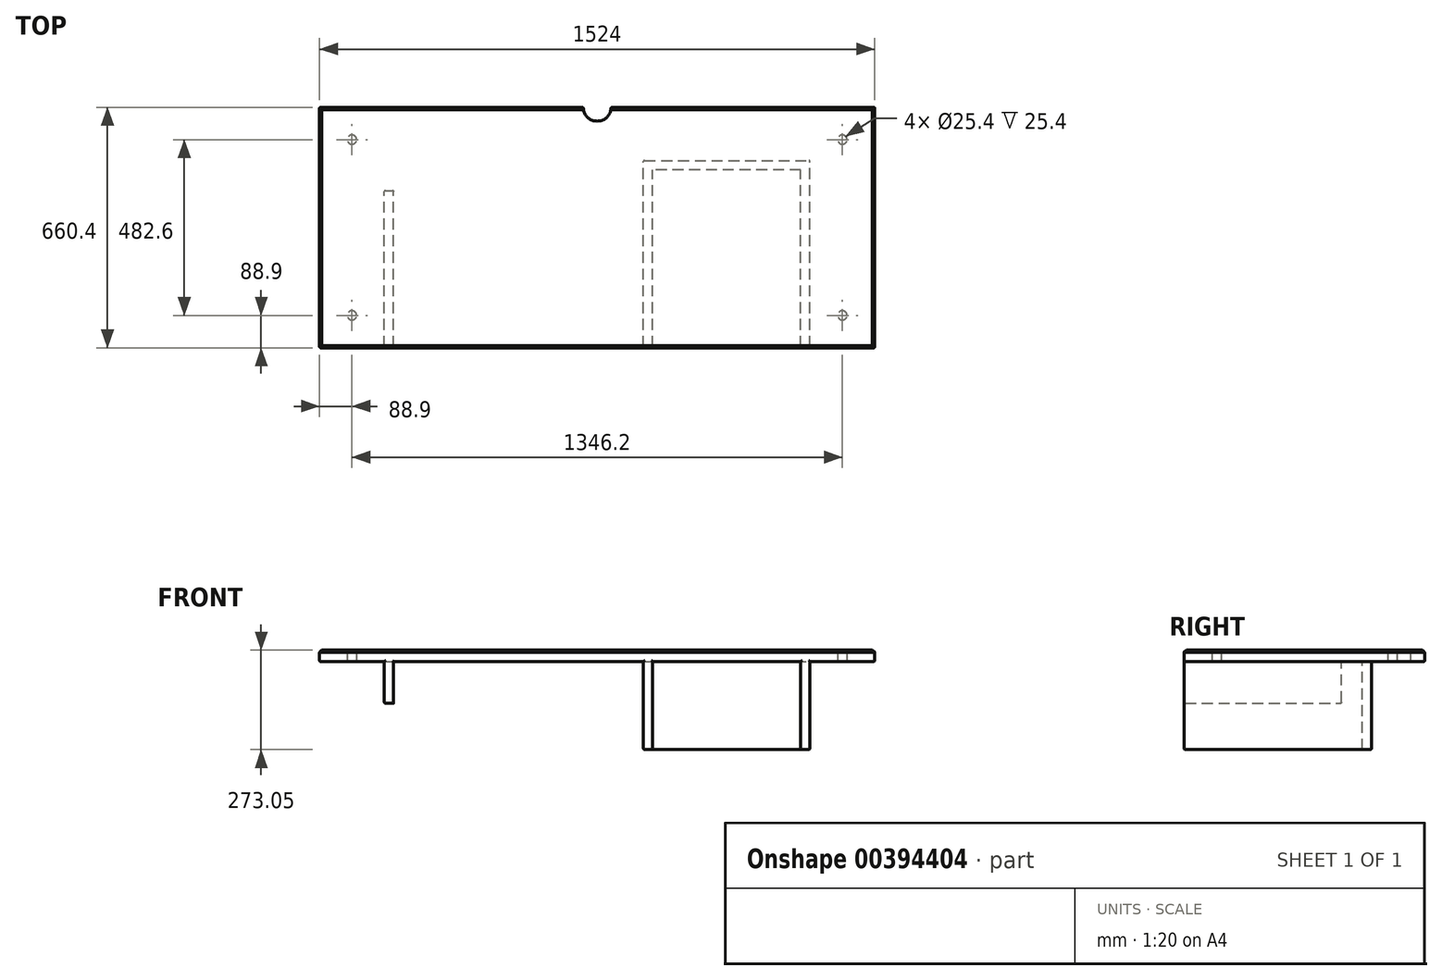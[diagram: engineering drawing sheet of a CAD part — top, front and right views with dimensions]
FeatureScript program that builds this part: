
annotation { "Feature Type Name" : "Feature", "Feature Type Description" : "" }
export const myFeature = defineFeature(function(context is Context, id is Id, definition is map)
    precondition{}
    {
        {
            var Q0;
            Q0=qCreatedBy(makeId("Top.planeOp"),FACE);
            var sketch = newSketch(context, id + "F0", { "sketchPlane" : qUnion([Q0])});
            skLineSegment(sketch, "E0.bottom", {"start": v(-762, 330.2) * mm, "end": v(762, 330.2) * mm});
            skLineSegment(sketch, "E0.top", {"start": v(-762, -330.2) * mm, "end": v(762, -330.2) * mm});
            skLineSegment(sketch, "E0.left", {"start": v(-762, 330.2) * mm, "end": v(-762, -330.2) * mm});
            skLineSegment(sketch, "E0.right", {"start": v(762, 330.2) * mm, "end": v(762, -330.2) * mm});
            skPoint(sketch, "E0.middle", {"position": v(0, 0) * mm});
            skSolve(sketch);
        }
        {
            var Q0;
            Q0 = qSketchRegion(id + "F0", true);
            extrude(context, id + "F1", {"entities" : qUnion([Q0]), "oppositeDirection" : true, "depth" : 31.75 * mm});
        }
        {
            var Q0;
            Q0=makeQuery(id+"F1.opExtrude","CAP_FACE",FACE,{"disambiguationData":[OSD([sQuery(id+"F0.wireOp",EDGE,"E0.bottom"),sQuery(id+"F0.wireOp",EDGE,"E0.top"),sQuery(id+"F0.wireOp",EDGE,"E0.left"),sQuery(id+"F0.wireOp",EDGE,"E0.right")])],"isStart":true});
            var sketch = newSketch(context, id + "F2", { "sketchPlane" : qUnion([Q0])});
            skCircle(sketch, "E1", {"center": v(0, 330.2) * mm, "radius": 38.1 * mm});
            skSolve(sketch);
        }
        {
            var Q0;
            Q0 = qSketchRegion(id + "F2", true);
            extrude(context, id + "F3", {"entities" : qUnion([Q0]), "operationType" : NewBodyOperationType.REMOVE, "endBound" : BoundingType.THROUGH_ALL, "oppositeDirection" : true, "depth" : 25.4 * mm});
        }
        {
            var Q0;
            Q0=makeQuery(id+"F1.opExtrude","CAP_FACE",FACE,{"disambiguationData":[OSD([sQuery(id+"F0.wireOp",EDGE,"E0.bottom"),sQuery(id+"F0.wireOp",EDGE,"E0.top"),sQuery(id+"F0.wireOp",EDGE,"E0.left"),sQuery(id+"F0.wireOp",EDGE,"E0.right")])],"isStart":false});
            var sketch = newSketch(context, id + "F4", { "sketchPlane" : qUnion([Q0])});
            skLineSegment(sketch, "E2.bottom", {"start": v(-584.2, 330.2) * mm, "end": v(-558.8, 330.2) * mm});
            skLineSegment(sketch, "E2.top", {"start": v(-584.2, -101.6) * mm, "end": v(-558.8, -101.6) * mm});
            skLineSegment(sketch, "E2.left", {"start": v(-584.2, 330.2) * mm, "end": v(-584.2, -101.6) * mm});
            skLineSegment(sketch, "E2.right", {"start": v(-558.8, 330.2) * mm, "end": v(-558.8, -101.6) * mm});
            skPoint(sketch, "E3.oppositeSnap0", {"position": v(-571.5, -101.6) * mm});
            skSolve(sketch);
        }
        {
            var Q0;
            Q0 = qSketchRegion(id + "F4", true);
            extrude(context, id + "F5", {"entities" : qUnion([Q0]), "operationType" : NewBodyOperationType.ADD, "depth" : 114.3 * mm});
        }
        {
            var Q0;
            {var subQ0=sQuery(id+"F0.wireOp",EDGE,"E0.bottom");var subQ1=sQuery(id+"F0.wireOp",EDGE,"E0.right");Q0=makeQuery(id+"F3.boolean.opBoolean","SPLIT",EDGE,{"disambiguationData":[TD([makeQuery(id+"F1.opExtrude","SWEPT_FACE",FACE,{"disambiguationData":[OSD([subQ1])]})])],"derivedFrom":makeQuery(id+"F1.opExtrude","CAP_EDGE",EDGE,{"disambiguationData":[OSD([subQ0])],"isStart":true})});}
            var Q1;
            Q1=makeQuery(id+"F1.opExtrude","CAP_EDGE",EDGE,{"disambiguationData":[OSD([sQuery(id+"F0.wireOp",EDGE,"E0.right")])],"isStart":true});
            var Q2;
            {var subQ0=sQuery(id+"F0.wireOp",EDGE,"E0.bottom");var subQ1=sQuery(id+"F0.wireOp",EDGE,"E0.left");Q2=makeQuery(id+"F3.boolean.opBoolean","SPLIT",EDGE,{"disambiguationData":[TD([makeQuery(id+"F1.opExtrude","SWEPT_FACE",FACE,{"disambiguationData":[OSD([subQ1])]})])],"derivedFrom":makeQuery(id+"F1.opExtrude","CAP_EDGE",EDGE,{"disambiguationData":[OSD([subQ0])],"isStart":true})});}
            var Q3;
            Q3=makeQuery(id+"F1.opExtrude","CAP_EDGE",EDGE,{"disambiguationData":[OSD([sQuery(id+"F0.wireOp",EDGE,"E0.left")])],"isStart":true});
            var Q4;
            Q4=makeQuery(id+"F1.opExtrude","CAP_EDGE",EDGE,{"disambiguationData":[OSD([sQuery(id+"F0.wireOp",EDGE,"E0.top")])],"isStart":true});
            var Q5;
            Q5=makeQuery(id+"F3.boolean.opBoolean","COPY",EDGE,{"derivedFrom":makeQuery(id+"F3.opExtrude","CAP_EDGE",EDGE,{"disambiguationData":[OSD([sQuery(id+"F2.wireOp",EDGE,"E1")])],"isStart":true})});
            chamfer(context, id + "F6", {"entities" : qUnion([Q0, Q1, Q2, Q3, Q4, Q5]), "width" : 6.35 * mm, "tangentPropagation" : true});
        }
        {
            var Q0;
            Q0=makeQuery(id+"F1.opExtrude","CAP_FACE",FACE,{"disambiguationData":[OSD([sQuery(id+"F0.wireOp",EDGE,"E0.bottom"),sQuery(id+"F0.wireOp",EDGE,"E0.top"),sQuery(id+"F0.wireOp",EDGE,"E0.left"),sQuery(id+"F0.wireOp",EDGE,"E0.right")])],"isStart":false});
            var sketch = newSketch(context, id + "F7", { "sketchPlane" : qUnion([Q0])});
            skCircle(sketch, "E4", {"center": v(-673.1, 241.3) * mm, "radius": 12.7 * mm});
            skCircle(sketch, "E5", {"center": v(-673.1, -241.3) * mm, "radius": 12.7 * mm});
            skCircle(sketch, "E6", {"center": v(673.1, 241.3) * mm, "radius": 12.7 * mm});
            skCircle(sketch, "E7", {"center": v(673.1, -241.3) * mm, "radius": 12.7 * mm});
            skSolve(sketch);
        }
        {
            var Q0;
            Q0 = qSketchRegion(id + "F7", true);
            extrude(context, id + "F8", {"entities" : qUnion([Q0]), "operationType" : NewBodyOperationType.REMOVE, "oppositeDirection" : true, "depth" : 25.4 * mm});
        }
        {
            var Q0;
            Q0=makeQuery(id+"F1.opExtrude","CAP_FACE",FACE,{"disambiguationData":[OSD([sQuery(id+"F0.wireOp",EDGE,"E0.bottom"),sQuery(id+"F0.wireOp",EDGE,"E0.top"),sQuery(id+"F0.wireOp",EDGE,"E0.left"),sQuery(id+"F0.wireOp",EDGE,"E0.right")])],"isStart":false});
            var sketch = newSketch(context, id + "F9", { "sketchPlane" : qUnion([Q0])});
            skLineSegment(sketch, "E8.bottom", {"start": v(127, 330.2) * mm, "end": v(152.4, 330.2) * mm});
            skLineSegment(sketch, "E8.top", {"start": v(127, -184.15) * mm, "end": v(152.4, -184.15) * mm});
            skLineSegment(sketch, "E8.left", {"start": v(127, 330.2) * mm, "end": v(127, -184.15) * mm});
            skLineSegment(sketch, "E8.right", {"start": v(152.4, 330.2) * mm, "end": v(152.4, -158.75) * mm});
            skLineSegment(sketch, "E9.bottom", {"start": v(558.8, 330.2) * mm, "end": v(584.2, 330.2) * mm});
            skLineSegment(sketch, "E9.top", {"start": v(558.8, -184.15) * mm, "end": v(584.2, -184.15) * mm});
            skLineSegment(sketch, "E9.left", {"start": v(558.8, 330.2) * mm, "end": v(558.8, -158.75) * mm});
            skLineSegment(sketch, "E9.right", {"start": v(584.2, 330.2) * mm, "end": v(584.2, -184.15) * mm});
            skLineSegment(sketch, "E10", {"start": v(584.2, -184.15) * mm, "end": v(127, -184.15) * mm});
            skLineSegment(sketch, "E11", {"start": v(558.8, -158.75) * mm, "end": v(152.4, -158.75) * mm});
            skSolve(sketch);
        }
        {
            var Q0;
            Q0 = qSketchRegion(id + "F9", true);
            extrude(context, id + "F10", {"entities" : qUnion([Q0]), "operationType" : NewBodyOperationType.ADD, "depth" : 241.3 * mm});
        }
        {
            var Q0;
            {var subQ0=sQuery(id+"F0.wireOp",EDGE,"E0.left");var subQ1=sQuery(id+"F0.wireOp",EDGE,"E0.top");Q0=makeQuery(id+"F5.boolean.opBoolean","SPLIT",EDGE,{"disambiguationData":[TD([makeQuery(id+"F1.opExtrude","SWEPT_FACE",FACE,{"disambiguationData":[OSD([subQ0])]})])],"derivedFrom":makeQuery(id+"F1.opExtrude","CAP_EDGE",EDGE,{"disambiguationData":[OSD([subQ1])],"isStart":false})});}
            var Q1;
            {var subQ0=sQuery(id+"F0.wireOp",EDGE,"E0.bottom");var subQ1=sQuery(id+"F0.wireOp",EDGE,"E0.right");Q1=makeQuery(id+"F3.boolean.opBoolean","SPLIT",EDGE,{"disambiguationData":[TD([makeQuery(id+"F1.opExtrude","SWEPT_FACE",FACE,{"disambiguationData":[OSD([subQ1])]})])],"derivedFrom":makeQuery(id+"F1.opExtrude","CAP_EDGE",EDGE,{"disambiguationData":[OSD([subQ0])],"isStart":false})});}
            var Q2;
            {var subQ0=sQuery(id+"F0.wireOp",EDGE,"E0.bottom");var subQ1=sQuery(id+"F0.wireOp",EDGE,"E0.left");Q2=makeQuery(id+"F3.boolean.opBoolean","SPLIT",EDGE,{"disambiguationData":[TD([makeQuery(id+"F1.opExtrude","SWEPT_FACE",FACE,{"disambiguationData":[OSD([subQ1])]})])],"derivedFrom":makeQuery(id+"F1.opExtrude","CAP_EDGE",EDGE,{"disambiguationData":[OSD([subQ0])],"isStart":false})});}
            var Q3;
            Q3=makeQuery(id+"F1.opExtrude","CAP_EDGE",EDGE,{"disambiguationData":[OSD([sQuery(id+"F0.wireOp",EDGE,"E0.left")])],"isStart":false});
            var Q4;
            Q4=makeQuery(id+"F1.opExtrude","CAP_EDGE",EDGE,{"disambiguationData":[OSD([sQuery(id+"F0.wireOp",EDGE,"E0.right")])],"isStart":false});
            var Q5;
            Q5=makeQuery(id+"F5.opExtrude","SWEPT_EDGE",EDGE,{"disambiguationData":[OSD([sQuery(id+"F0.wireOp",EDGE,"E0.top"),sQuery(id+"F4.wireOp",EDGE,"E2.bottom"),sQuery(id+"F4.wireOp",EDGE,"E2.left")])]});
            var Q6;
            Q6=makeQuery(id+"F5.opExtrude","SWEPT_EDGE",EDGE,{"disambiguationData":[OSD([sQuery(id+"F0.wireOp",EDGE,"E0.top"),sQuery(id+"F4.wireOp",EDGE,"E2.bottom"),sQuery(id+"F4.wireOp",EDGE,"E2.right")])]});
            var Q7;
            Q7=makeQuery(id+"F5.opExtrude","CAP_EDGE",EDGE,{"disambiguationData":[OSD([sQuery(id+"F4.wireOp",EDGE,"E2.bottom")])],"isStart":false});
            var Q8;
            Q8=makeQuery(id+"F5.opExtrude","SWEPT_EDGE",EDGE,{"disambiguationData":[OSD([sQuery(id+"F0.wireOp",EDGE,"E0.top"),sQuery(id+"F4.wireOp",EDGE,"E2.bottom"),sQuery(id+"F4.wireOp",EDGE,"E2.left")])]});
            var Q9;
            Q9=makeQuery(id+"F5.opExtrude","SWEPT_EDGE",EDGE,{"disambiguationData":[OSD([sQuery(id+"F0.wireOp",EDGE,"E0.top"),sQuery(id+"F4.wireOp",EDGE,"E2.bottom"),sQuery(id+"F4.wireOp",EDGE,"E2.right")])]});
            var Q10;
            Q10=makeQuery(id+"F5.opExtrude","SWEPT_EDGE",EDGE,{"disambiguationData":[OSD([sQuery(id+"F0.wireOp",EDGE,"E0.top"),sQuery(id+"F4.wireOp",EDGE,"E2.bottom"),sQuery(id+"F4.wireOp",EDGE,"E2.left")])]});
            var Q11;
            Q11=makeQuery(id+"F5.opExtrude","SWEPT_EDGE",EDGE,{"disambiguationData":[OSD([sQuery(id+"F0.wireOp",EDGE,"E0.top"),sQuery(id+"F4.wireOp",EDGE,"E2.bottom"),sQuery(id+"F4.wireOp",EDGE,"E2.right")])]});
            var Q12;
            Q12=makeQuery(id+"F5.opExtrude","SWEPT_EDGE",EDGE,{"disambiguationData":[OSD([sQuery(id+"F4.wireOp",EDGE,"E2.top"),sQuery(id+"F4.wireOp",EDGE,"E2.left")])]});
            var Q13;
            Q13=makeQuery(id+"F5.opExtrude","SWEPT_EDGE",EDGE,{"disambiguationData":[OSD([sQuery(id+"F4.wireOp",EDGE,"E2.top"),sQuery(id+"F4.wireOp",EDGE,"E2.right")])]});
            var Q14;
            Q14=makeQuery(id+"F5.opExtrude","CAP_EDGE",EDGE,{"disambiguationData":[OSD([sQuery(id+"F4.wireOp",EDGE,"E2.top")])],"isStart":false});
            var Q15;
            Q15=makeQuery(id+"F5.opExtrude","CAP_EDGE",EDGE,{"disambiguationData":[OSD([sQuery(id+"F4.wireOp",EDGE,"E2.left")])],"isStart":false});
            fillet(context, id + "F11", {"entities" : qUnion([Q0, Q1, Q2, Q3, Q4, Q5, Q6, Q7, Q8, Q9, Q10, Q11, Q12, Q13, Q14, Q15]), "radius" : 3.17 * mm, "tangentPropagation" : true, "allowEdgeOverflow" : false});
        }
        {
            var Q0;
            Q0=makeQuery(id+"F3.boolean.opBoolean","INTERSECT",EDGE,{"derivedFrom":[makeQuery(id+"F1.opExtrude","CAP_FACE",FACE,{"disambiguationData":[OSD([sQuery(id+"F0.wireOp",EDGE,"E0.bottom"),sQuery(id+"F0.wireOp",EDGE,"E0.top"),sQuery(id+"F0.wireOp",EDGE,"E0.left"),sQuery(id+"F0.wireOp",EDGE,"E0.right")])],"isStart":false}),makeQuery(id+"F3.opExtrude","SWEPT_FACE",FACE,{"disambiguationData":[OSD([sQuery(id+"F2.wireOp",EDGE,"E1")])]})]});
            var Q1;
            Q1=makeQuery(id+"F1.opExtrude","SWEPT_EDGE",EDGE,{"disambiguationData":[OSD([sQuery(id+"F0.wireOp",EDGE,"E0.bottom"),sQuery(id+"F0.wireOp",EDGE,"E0.left")])]});
            var Q2;
            Q2=makeQuery(id+"F1.opExtrude","SWEPT_EDGE",EDGE,{"disambiguationData":[OSD([sQuery(id+"F0.wireOp",EDGE,"E0.top"),sQuery(id+"F0.wireOp",EDGE,"E0.left")])]});
            var Q3;
            Q3=makeQuery(id+"F1.opExtrude","SWEPT_EDGE",EDGE,{"disambiguationData":[OSD([sQuery(id+"F0.wireOp",EDGE,"E0.top"),sQuery(id+"F0.wireOp",EDGE,"E0.right")])]});
            var Q4;
            Q4=makeQuery(id+"F1.opExtrude","SWEPT_EDGE",EDGE,{"disambiguationData":[OSD([sQuery(id+"F0.wireOp",EDGE,"E0.bottom"),sQuery(id+"F0.wireOp",EDGE,"E0.right")])]});
            var Q5;
            Q5=makeQuery(id+"F10.opExtrude","SWEPT_EDGE",EDGE,{"disambiguationData":[OSD([sQuery(id+"F0.wireOp",EDGE,"E0.top"),sQuery(id+"F9.wireOp",EDGE,"E8.bottom"),sQuery(id+"F9.wireOp",EDGE,"E8.left")])]});
            var Q6;
            Q6=makeQuery(id+"F10.opExtrude","CAP_EDGE",EDGE,{"disambiguationData":[OSD([sQuery(id+"F9.wireOp",EDGE,"E8.left")])],"isStart":false});
            var Q7;
            Q7=makeQuery(id+"F10.opExtrude","SWEPT_EDGE",EDGE,{"disambiguationData":[OSD([sQuery(id+"F0.wireOp",EDGE,"E0.top"),sQuery(id+"F9.wireOp",EDGE,"E8.bottom"),sQuery(id+"F9.wireOp",EDGE,"E8.right")])]});
            var Q8;
            Q8=makeQuery(id+"F10.opExtrude","CAP_EDGE",EDGE,{"disambiguationData":[OSD([sQuery(id+"F9.wireOp",EDGE,"E8.top")])],"isStart":false});
            var Q9;
            {var subQ0=sQuery(id+"F0.wireOp",EDGE,"E0.top");var subQ2=makeQuery(id+"F5.opExtrude","SWEPT_FACE",FACE,{"disambiguationData":[OSD([sQuery(id+"F4.wireOp",EDGE,"E2.right")])]});var subQ4=sQuery(id+"F0.wireOp",EDGE,"E0.right");Q9=makeQuery(id+"F10.boolean.opBoolean","SPLIT",EDGE,{"disambiguationData":[TD([subQ2])],"derivedFrom":makeQuery(id+"F5.boolean.opBoolean","SPLIT",EDGE,{"disambiguationData":[TD([makeQuery(id+"F1.opExtrude","SWEPT_FACE",FACE,{"disambiguationData":[OSD([subQ4])]})])],"derivedFrom":makeQuery(id+"F1.opExtrude","CAP_EDGE",EDGE,{"disambiguationData":[OSD([subQ0])],"isStart":false})})});}
            var Q10;
            Q10=makeQuery(id+"F10.opExtrude","CAP_EDGE",EDGE,{"disambiguationData":[OSD([sQuery(id+"F9.wireOp",EDGE,"E8.bottom")])],"isStart":false});
            var Q11;
            Q11=makeQuery(id+"F10.opExtrude","SWEPT_EDGE",EDGE,{"disambiguationData":[OSD([sQuery(id+"F0.wireOp",EDGE,"E0.top"),sQuery(id+"F9.wireOp",EDGE,"E9.bottom"),sQuery(id+"F9.wireOp",EDGE,"E9.left")])]});
            var Q12;
            Q12=makeQuery(id+"F10.opExtrude","SWEPT_EDGE",EDGE,{"disambiguationData":[OSD([sQuery(id+"F0.wireOp",EDGE,"E0.top"),sQuery(id+"F9.wireOp",EDGE,"E9.bottom"),sQuery(id+"F9.wireOp",EDGE,"E9.right")])]});
            var Q13;
            Q13=makeQuery(id+"F10.opExtrude","CAP_EDGE",EDGE,{"disambiguationData":[OSD([sQuery(id+"F9.wireOp",EDGE,"E9.bottom")])],"isStart":false});
            var Q14;
            Q14=makeQuery(id+"F10.opExtrude","SWEPT_EDGE",EDGE,{"disambiguationData":[OSD([sQuery(id+"F9.wireOp",EDGE,"E9.top"),sQuery(id+"F9.wireOp",EDGE,"E9.right")])]});
            var Q15;
            Q15=makeQuery(id+"F10.opExtrude","SWEPT_EDGE",EDGE,{"disambiguationData":[OSD([sQuery(id+"F9.wireOp",EDGE,"E8.top"),sQuery(id+"F9.wireOp",EDGE,"E8.left")])]});
            var Q16;
            Q16=makeQuery(id+"F10.opExtrude","CAP_EDGE",EDGE,{"disambiguationData":[OSD([sQuery(id+"F9.wireOp",EDGE,"E9.top")])],"isStart":false});
            var Q17;
            Q17=makeQuery(id+"F10.opExtrude","CAP_EDGE",EDGE,{"disambiguationData":[OSD([sQuery(id+"F9.wireOp",EDGE,"E9.right")])],"isStart":false});
            var Q18;
            {var subQ0=sQuery(id+"F0.wireOp",EDGE,"E0.top");var subQ3=sQuery(id+"F0.wireOp",EDGE,"E0.right");Q18=makeQuery(id+"F10.boolean.opBoolean","SPLIT",EDGE,{"disambiguationData":[TD([makeQuery(id+"F10.opExtrude","SWEPT_FACE",FACE,{"disambiguationData":[OSD([sQuery(id+"F9.wireOp",EDGE,"E8.right")])]})])],"derivedFrom":makeQuery(id+"F5.boolean.opBoolean","SPLIT",EDGE,{"disambiguationData":[TD([makeQuery(id+"F1.opExtrude","SWEPT_FACE",FACE,{"disambiguationData":[OSD([subQ3])]})])],"derivedFrom":makeQuery(id+"F1.opExtrude","CAP_EDGE",EDGE,{"disambiguationData":[OSD([subQ0])],"isStart":false})})});}
            var Q19;
            Q19=makeQuery(id+"F10.opExtrude","CAP_EDGE",EDGE,{"disambiguationData":[OSD([sQuery(id+"F9.wireOp",EDGE,"E10")])],"isStart":false});
            fillet(context, id + "F12", {"entities" : qUnion([Q0, Q1, Q2, Q3, Q4, Q5, Q6, Q7, Q8, Q9, Q10, Q11, Q12, Q13, Q14, Q15, Q16, Q17, Q18, Q19]), "radius" : 3.17 * mm, "tangentPropagation" : true, "allowEdgeOverflow" : false});
        }
    });
